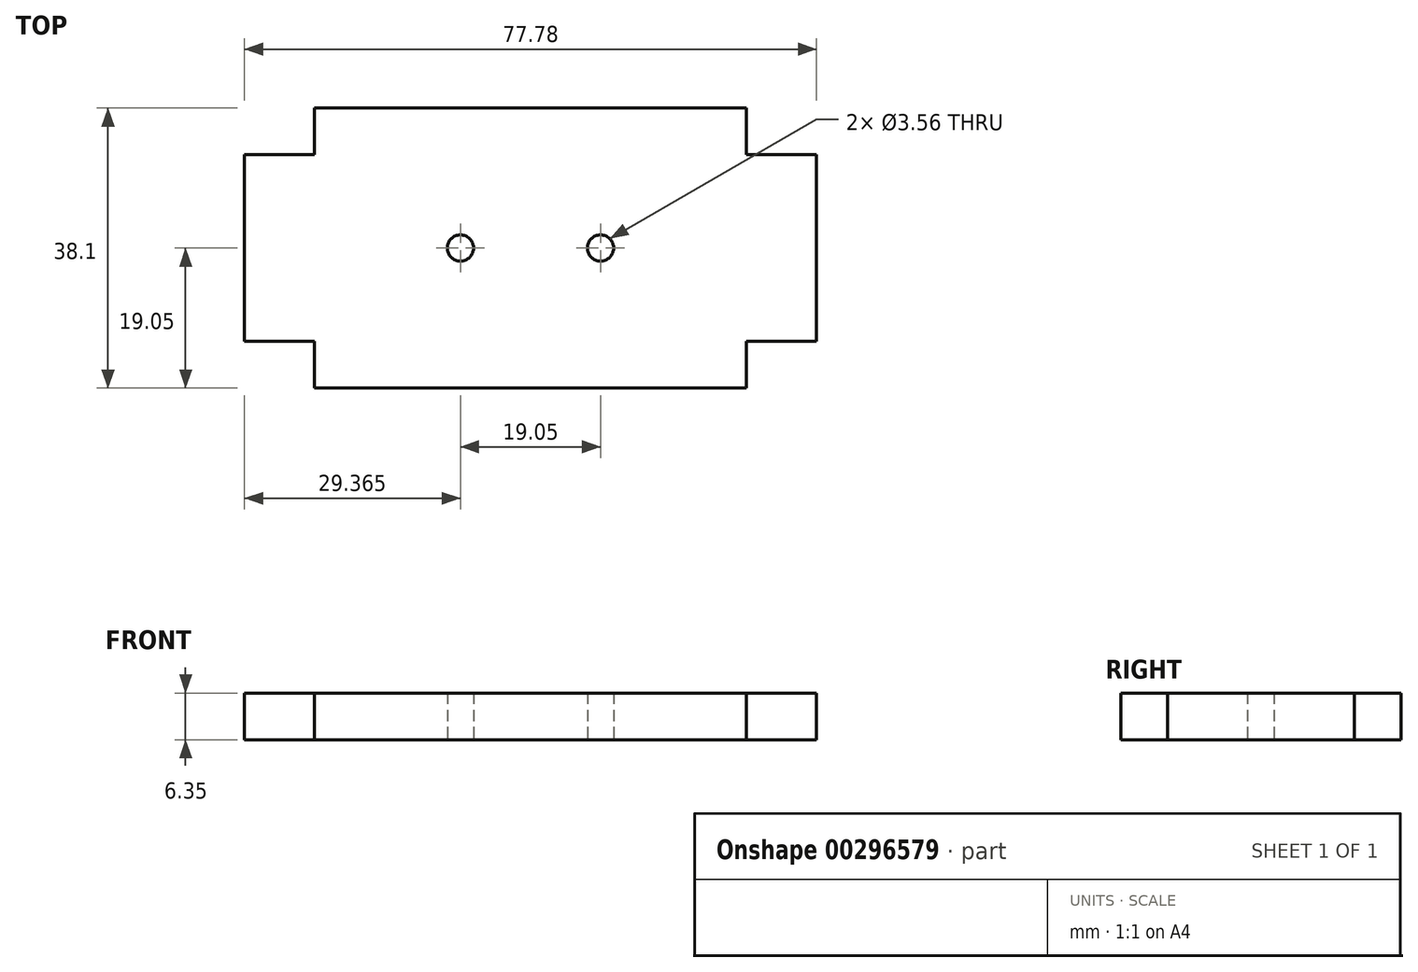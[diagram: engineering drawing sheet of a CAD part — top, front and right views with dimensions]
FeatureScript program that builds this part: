
annotation { "Feature Type Name" : "Feature", "Feature Type Description" : "" }
export const myFeature = defineFeature(function(context is Context, id is Id, definition is map)
    precondition{}
    {
        {
            var Q0;
            Q0=qCreatedBy(makeId("Top.planeOp"),FACE);
            var sketch = newSketch(context, id + "F0", { "sketchPlane" : qUnion([Q0])});
            skLineSegment(sketch, "E0.bottom", {"start": v(38.9, -12.7) * mm, "end": v(29.37, -12.7) * mm});
            skLineSegment(sketch, "E0.top", {"start": v(38.9, 12.7) * mm, "end": v(29.37, 12.7) * mm});
            skLineSegment(sketch, "E0.left", {"start": v(38.9, -12.7) * mm, "end": v(38.9, 12.7) * mm});
            skLineSegment(sketch, "E0.right", {"start": v(-38.9, -12.7) * mm, "end": v(-38.9, 12.7) * mm});
            skPoint(sketch, "E0.middle", {"position": v(0, 0) * mm});
            skLineSegment(sketch, "E1.bottom", {"start": v(29.37, -19.05) * mm, "end": v(-29.37, -19.05) * mm});
            skLineSegment(sketch, "E1.top", {"start": v(29.37, 19.05) * mm, "end": v(-29.37, 19.05) * mm});
            skLineSegment(sketch, "E1.left", {"start": v(29.37, -19.05) * mm, "end": v(29.37, -12.7) * mm});
            skLineSegment(sketch, "E1.right", {"start": v(-29.37, -19.05) * mm, "end": v(-29.37, -12.7) * mm});
            skLineSegment(sketch, "E2.trimOffspring", {"start": v(-29.37, 12.7) * mm, "end": v(-38.9, 12.7) * mm});
            skLineSegment(sketch, "E3.trimOffspring", {"start": v(-29.37, 12.7) * mm, "end": v(-29.37, 19.05) * mm});
            skLineSegment(sketch, "E4.trimOffspring", {"start": v(-29.37, -12.7) * mm, "end": v(-38.9, -12.7) * mm});
            skLineSegment(sketch, "E5.trimOffspring", {"start": v(29.37, 12.7) * mm, "end": v(29.37, 19.05) * mm});
            skCircle(sketch, "E6", {"center": v(-9.53, 0) * mm, "radius": 1.78 * mm});
            skCircle(sketch, "E7", {"center": v(9.53, 0) * mm, "radius": 1.78 * mm});
            skLineSegment(sketch, "E8", {"start": v(0, 0) * mm, "end": v(0, 19.05) * mm, "construction": true});
            skSolve(sketch);
        }
        {
            var Q0;
            Q0 = qSketchRegion(id + "F0", true);
            extrude(context, id + "F1", {"entities" : qUnion([Q0]), "depth" : 6.35 * mm});
        }
    });
